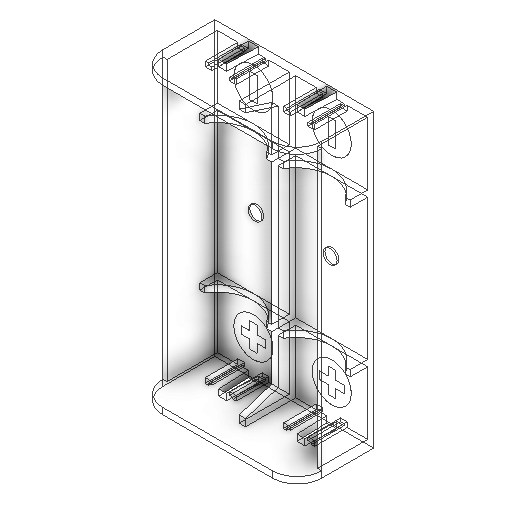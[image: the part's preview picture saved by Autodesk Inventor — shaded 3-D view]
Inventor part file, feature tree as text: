
AUTODESK INVENTOR PART (.ipt)
format: ipt  version: 2025.2 (Build 292293000, 293)  size: 449,024 bytes
history: native  units: mm
features: sketch x10, extrude x9, mirror x3, plane x1, hole x1
ambient origin geometry x8: Origin, YZ Plane, XZ Plane, XY Plane, X Axis, Y Axis, Z Axis, Center Point
bodies: Solid1 (feature_tree)
feature tree (24):
  extrude  "Extrusion1"  Depth=45.2mm
  extrude  "Extrusion2"  Depth=83.0mm TaperAngle=0.0deg
  extrude  "Extrusion3"  Depth=1.2mm
  extrude  "Extrusion4"  Depth=21.3mm TaperAngle=0.0deg
  plane  "Work Plane1"
  extrude  "Extrusion5"  Depth=5.0mm
  mirror  "Mirror1"
  mirror  "Mirror2"
  extrude  "Extrusion6"  Depth=1.8mm TaperAngle=0.0deg
  extrude  "Extrusion7"  Depth=0.9mm
  extrude  "Extrusion8"  Depth=7.0mm
  hole  "Hole1"  [1 undecoded]
  extrude  "Extrusion9"  Depth=0.01mm
  mirror  "Mirror3"
  sketch  "Sketch1"  dims[d0=21.8mm d1=45.2mm]
  sketch  "Sketch2"  dims[d2=7.0mm d3=83.0mm d4=0.0mm]
  sketch  "Sketch3"  dims[d5=1.8mm d6=1.2mm]
  sketch  "Sketch4"  dims[d7=21.3mm d8=0.0mm d9=21.3mm d10=0.0mm]
  sketch  "Sketch5"  dims[d11=2.0mm d12=5.0mm]
  sketch  "Sketch6"  dims[d13=5.0mm d14=1.8mm d15=0.0mm]
  sketch  "Sketch7"  dims[d16=9.8mm d17=0.9mm]
  sketch  "Sketch8"  dims[d18=0.9mm d19=7.0mm]
  sketch  "Sketch9"  dims[d20=0.5mm d21=5.0mm]
  sketch  "Sketch10"  dims[d22=1.8mm d23=0.0mm d24=2.22mm d25=2.88mm d26=8.75mm d27=0.0mm d28=0.0mm d29=1.8mm d30=40.0mm d31=10.0mm d32=0.0mm d33=20.5mm d34=50.0mm d35=0.0mm d36=4.0mm d37=6.0mm d38=4.0mm d39=2.0mm d40=90.0deg d41=1.0mm d42=20.594885mm d43=21.39mm d44=7.0mm d45=7.0mm d46=0.01mm d47=0.0mm]
note: 1 required parameter value undecoded (feature->parameter linkage not recoverable at this tier; creation-order binding heuristic only, values carry confidence <= 0.55)
